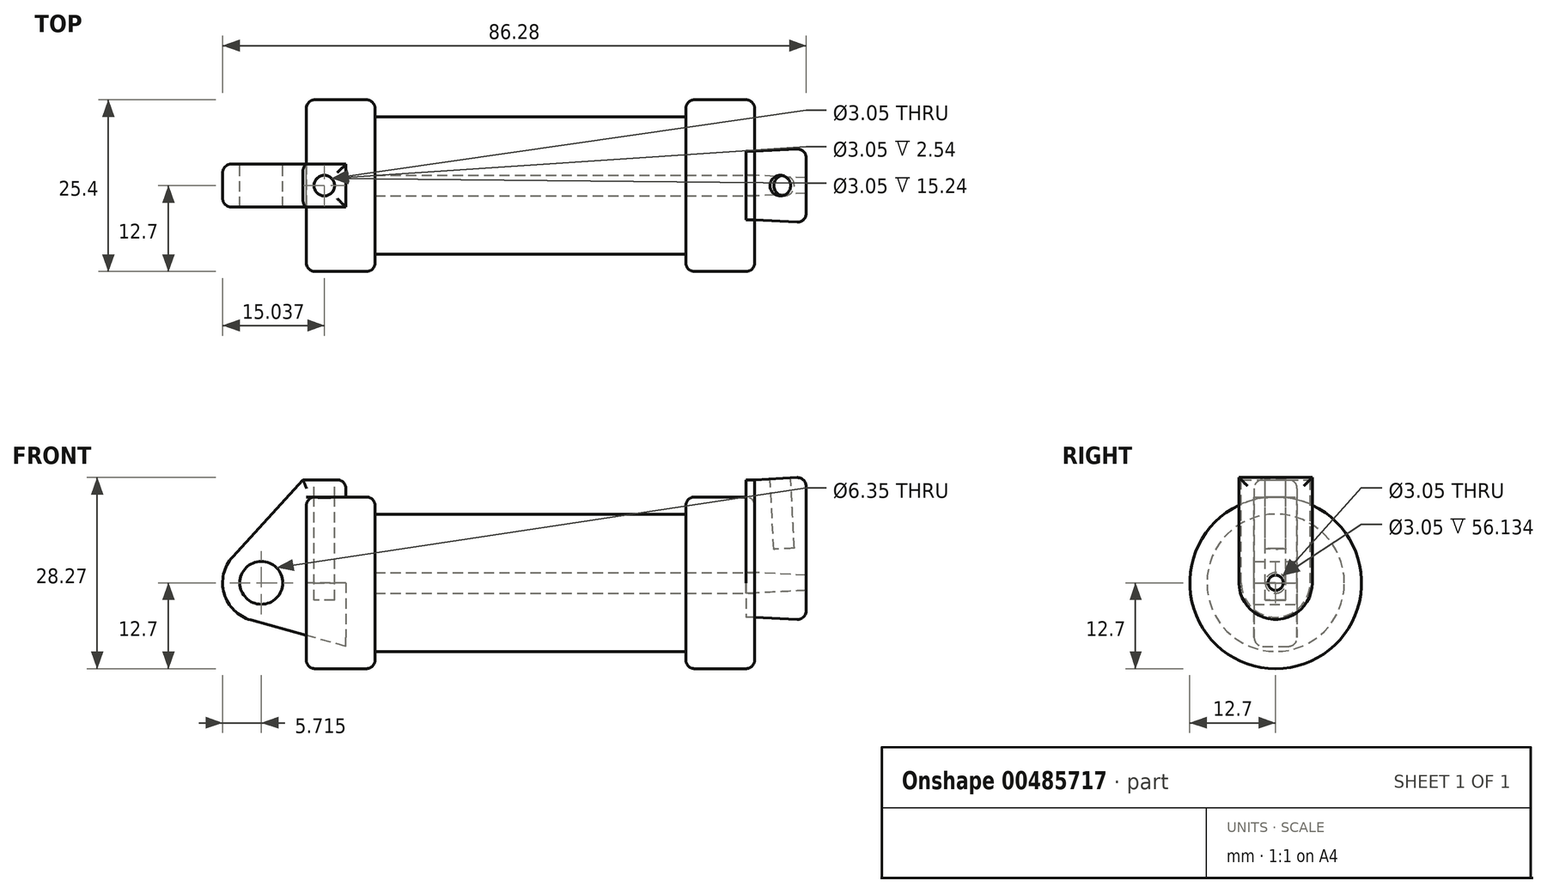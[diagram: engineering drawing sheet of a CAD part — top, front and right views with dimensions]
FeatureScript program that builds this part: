
annotation { "Feature Type Name" : "Feature", "Feature Type Description" : "" }
export const myFeature = defineFeature(function(context is Context, id is Id, definition is map)
    precondition{}
    {
        {
            var Q0;
            Q0=qCreatedBy(makeId("Front.planeOp"),FACE);
            var sketch = newSketch(context, id + "F0", { "sketchPlane" : qUnion([Q0])});
            skLineSegment(sketch, "E0", {"start": v(0, 0) * mm, "end": v(0, 12.7) * mm});
            skLineSegment(sketch, "E1", {"start": v(0, 12.7) * mm, "end": v(10.16, 12.7) * mm});
            skLineSegment(sketch, "E2", {"start": v(10.16, 12.7) * mm, "end": v(10.16, 10.16) * mm});
            skLineSegment(sketch, "E3", {"start": v(10.16, 10.16) * mm, "end": v(56.13, 10.16) * mm});
            skLineSegment(sketch, "E4", {"start": v(56.13, 10.16) * mm, "end": v(56.13, 12.7) * mm});
            skLineSegment(sketch, "E5", {"start": v(56.13, 12.7) * mm, "end": v(66.3, 12.7) * mm});
            skLineSegment(sketch, "E6", {"start": v(66.3, 12.7) * mm, "end": v(66.3, 0) * mm});
            skLineSegment(sketch, "E7", {"start": v(66.3, 0) * mm, "end": v(0, 0) * mm});
            skLineSegment(sketch, "E8", {"start": v(5.84, 15.24) * mm, "end": v(-0.5, 15.24) * mm});
            skLineSegment(sketch, "E9", {"start": v(-0.5, 15.24) * mm, "end": v(-10.88, 3.85) * mm});
            skLineSegment(sketch, "E10", {"start": v(0, 0) * mm, "end": v(-6.65, 0) * mm});
            skCircle(sketch, "E11", {"center": v(-6.65, 0) * mm, "radius": 5.72 * mm});
            skCircle(sketch, "E12", {"center": v(-6.65, 0) * mm, "radius": 3.18 * mm});
            skLineSegment(sketch, "E13", {"start": v(5.84, 15.24) * mm, "end": v(5.84, -9.4) * mm});
            skLineSegment(sketch, "E14", {"start": v(5.84, -9.4) * mm, "end": v(-8.18, -5.5) * mm});
            skSolve(sketch);
        }
        {
            var Q0;
            {var subQ0=sQuery(id+"F0.wireOp",EDGE,"E2");Q0=makeQuery(id+"F0.imprint","IMPRINT",FACE,{"disambiguationData":[TD([[makeQuery(id+"F0.imprint","IMPRINT",EDGE,{"derivedFrom":subQ0}),-1.0]])]});}
            var Q1;
            {var subQ0=sQuery(id+"F0.wireOp",EDGE,"E0");Q1=makeQuery(id+"F0.imprint","IMPRINT",FACE,{"disambiguationData":[TD([[makeQuery(id+"F0.imprint","IMPRINT",EDGE,{"derivedFrom":subQ0}),-1.0]])]});}
            var Q2;
            Q2=sQuery(id+"F0.wireOp",EDGE,"E7");
            revolve(context, id + "F1", {"entities" : qUnion([Q0, Q1]), "axis" : qUnion([Q2]), "revolveType" : RevolveType.FULL});
        }
        {
            var Q0;
            {var subQ5=sQuery(id+"F0.wireOp",EDGE,"E12");Q0=makeQuery(id+"F0.imprint","IMPRINT",FACE,{"disambiguationData":[TD([[makeQuery(id+"F0.imprint","IMPRINT",EDGE,{"derivedFrom":subQ5}),-1.0]])]});}
            var Q1;
            {var subQ1=sQuery(id+"F0.wireOp",EDGE,"E0");Q1=makeQuery(id+"F0.imprint","IMPRINT",FACE,{"disambiguationData":[TD([[makeQuery(id+"F0.imprint","IMPRINT",EDGE,{"derivedFrom":subQ1}),1.0]])]});}
            var Q2;
            {var subQ0=sQuery(id+"F0.wireOp",EDGE,"E14");Q2=makeQuery(id+"F0.imprint","IMPRINT",FACE,{"disambiguationData":[TD([[makeQuery(id+"F0.imprint","IMPRINT",EDGE,{"derivedFrom":subQ0}),-1.0]])]});}
            extrude(context, id + "F2", {"entities" : qUnion([Q0, Q1, Q2]), "endBound" : BoundingType.SYMMETRIC, "depth" : 6.35 * mm});
        }
        {
            var Q0;
            Q0=makeQuery(id+"F1.opRevolve","SWEPT_FACE",FACE,{"disambiguationData":[OSD([sQuery(id+"F0.wireOp",EDGE,"E6")])]});
            var sketch = newSketch(context, id + "F3", { "sketchPlane" : qUnion([Q0])});
            skCircle(sketch, "E15", {"center": v(0, 0) * mm, "radius": 1.52 * mm});
            skCircle(sketch, "E16", {"center": v(0, 0) * mm, "radius": 5.08 * mm});
            skLineSegment(sketch, "E17", {"start": v(-5.08, 0) * mm, "end": v(-5.08, 15.24) * mm});
            skLineSegment(sketch, "E18", {"start": v(-5.08, 15.24) * mm, "end": v(5.08, 15.24) * mm});
            skLineSegment(sketch, "E19", {"start": v(5.08, 15.24) * mm, "end": v(5.08, 0) * mm});
            skSolve(sketch);
        }
        {
            var Q0;
            Q0=makeQuery(id+"F3.imprint","IMPRINT",FACE,{"disambiguationData":[TD([[makeQuery(id+"F3.imprint","IMPRINT",EDGE,{"derivedFrom":sQuery(id+"F3.wireOp",EDGE,"E15")}),-1.0]])]});
            var Q1;
            {var subQ0=sQuery(id+"F3.wireOp",EDGE,"E17");var subQ1=sQuery(id+"F3.wireOp",EDGE,"E16");var subQ2=makeQuery(id+"F3.imprint","INTERSECT",VERTEX,{"derivedFrom":[subQ1,subQ0]});Q1=makeQuery(id+"F3.imprint","IMPRINT",FACE,{"disambiguationData":[TD([[makeQuery(id+"F3.imprint","IMPRINT",EDGE,{"disambiguationData":[TD([[subQ2,1.0]])],"derivedFrom":subQ1}),-1.0]])]});}
            var Q2;
            {var subQ0=sQuery(id+"F3.wireOp",EDGE,"E18");Q2=makeQuery(id+"F3.imprint","IMPRINT",FACE,{"disambiguationData":[TD([[makeQuery(id+"F3.imprint","IMPRINT",EDGE,{"derivedFrom":subQ0}),-1.0]])]});}
            extrude(context, id + "F4", {"entities" : qUnion([Q0, Q1, Q2]), "depth" : 7.62 * mm, "hasDraft" : true, "draftAngle" : 3 * degree, "hasSecondDirection" : true, "secondDirectionOppositeDirection" : true, "secondDirectionDepth" : 1.27 * mm});
        }
        {
            var Q0;
            Q0=makeQuery(id+"F3.imprint","IMPRINT",FACE,{"disambiguationData":[TD([[makeQuery(id+"F3.imprint","IMPRINT",EDGE,{"derivedFrom":sQuery(id+"F3.wireOp",EDGE,"E15")}),1.0]])]});
            var Q1;
            Q1=makeQuery(id+"F1.opRevolve","SWEPT_FACE",FACE,{"disambiguationData":[OSD([sQuery(id+"F0.wireOp",EDGE,"E2")])]});
            extrude(context, id + "F5", {"entities" : qUnion([Q0]), "operationType" : NewBodyOperationType.REMOVE, "endBound" : BoundingType.UP_TO_SURFACE, "oppositeDirection" : true, "endBoundEntityFace" : qUnion([Q1]), "depth" : 25.4 * mm});
        }
        {
            var Q0;
            Q0=makeQuery(id+"F4.*.split.splitOp","SPLIT",FACE,{"derivedFrom":makeQuery(id+"F4.opExtrude","SWEPT_FACE",FACE,{"disambiguationData":[OSD([sQuery(id+"F3.wireOp",EDGE,"E18")])]})});
            var sketch = newSketch(context, id + "F6", { "sketchPlane" : qUnion([Q0])});
            skCircle(sketch, "E20", {"center": v(70.82, 0) * mm, "radius": 1.52 * mm});
            skPoint(sketch, "E20.centerSnap0", {"position": v(70.82, 5.28) * mm});
            skPoint(sketch, "E20.centerSnap1", {"position": v(74.63, 0) * mm});
            skSolve(sketch);
        }
        {
            var Q0;
            Q0=makeQuery(id+"F6.imprint","IMPRINT",FACE,{"disambiguationData":[TD([[makeQuery(id+"F6.imprint","IMPRINT",EDGE,{"derivedFrom":sQuery(id+"F6.wireOp",EDGE,"E20")}),1.0]])]});
            extrude(context, id + "F7", {"entities" : qUnion([Q0]), "operationType" : NewBodyOperationType.REMOVE, "oppositeDirection" : true, "depth" : 10.4 * mm});
        }
        {
            var Q0;
            Q0=makeQuery(id+"F2.opExtrude","SWEPT_FACE",FACE,{"disambiguationData":[OSD([sQuery(id+"F0.wireOp",EDGE,"E8")])]});
            var sketch = newSketch(context, id + "F8", { "sketchPlane" : qUnion([Q0])});
            skCircle(sketch, "E21", {"center": v(2.67, 0) * mm, "radius": 1.52 * mm});
            skPoint(sketch, "E21.centerSnap0", {"position": v(2.67, 3.18) * mm});
            skPoint(sketch, "E21.centerSnap1", {"position": v(5.84, 0) * mm});
            skSolve(sketch);
        }
        {
            var Q0;
            Q0=makeQuery(id+"F8.imprint","IMPRINT",FACE,{"disambiguationData":[TD([[makeQuery(id+"F8.imprint","IMPRINT",EDGE,{"derivedFrom":sQuery(id+"F8.wireOp",EDGE,"E21")}),1.0]])]});
            extrude(context, id + "F9", {"entities" : qUnion([Q0]), "operationType" : NewBodyOperationType.REMOVE, "oppositeDirection" : true, "depth" : 17.78 * mm});
        }
        {
            var Q0;
            Q0=makeQuery(id+"F1.opRevolve","SWEPT_EDGE",EDGE,{"disambiguationData":[OSD([sQuery(id+"F0.wireOp",EDGE,"E1"),sQuery(id+"F0.wireOp",EDGE,"E2")])]});
            var Q1;
            Q1=makeQuery(id+"F1.opRevolve","SWEPT_EDGE",EDGE,{"disambiguationData":[OSD([sQuery(id+"F0.wireOp",EDGE,"E0"),sQuery(id+"F0.wireOp",EDGE,"E1")])]});
            var Q2;
            Q2=makeQuery(id+"F2.opExtrude","CAP_EDGE",EDGE,{"disambiguationData":[OSD([sQuery(id+"F0.wireOp",EDGE,"E8")])],"isStart":false});
            var Q3;
            Q3=makeQuery(id+"F2.opExtrude","SWEPT_EDGE",EDGE,{"disambiguationData":[OSD([sQuery(id+"F0.wireOp",EDGE,"E8"),sQuery(id+"F0.wireOp",EDGE,"E13")])]});
            var Q4;
            Q4=makeQuery(id+"F2.opExtrude","CAP_EDGE",EDGE,{"disambiguationData":[OSD([sQuery(id+"F0.wireOp",EDGE,"E8")])],"isStart":true});
            var Q5;
            Q5=makeQuery(id+"F2.opExtrude","CAP_EDGE",EDGE,{"disambiguationData":[OSD([sQuery(id+"F0.wireOp",EDGE,"E9")])],"isStart":false});
            var Q6;
            Q6=makeQuery(id+"F2.opExtrude","CAP_EDGE",EDGE,{"disambiguationData":[OSD([sQuery(id+"F0.wireOp",EDGE,"E9")])],"isStart":true});
            var Q7;
            Q7=makeQuery(id+"F1.opRevolve","SWEPT_EDGE",EDGE,{"disambiguationData":[OSD([sQuery(id+"F0.wireOp",EDGE,"E4"),sQuery(id+"F0.wireOp",EDGE,"E5")])]});
            var Q8;
            Q8=makeQuery(id+"F1.opRevolve","SWEPT_EDGE",EDGE,{"disambiguationData":[OSD([sQuery(id+"F0.wireOp",EDGE,"E5"),sQuery(id+"F0.wireOp",EDGE,"E6")])]});
            var Q9;
            Q9=makeQuery(id+"F4.opExtrude","CAP_EDGE",EDGE,{"disambiguationData":[OSD([sQuery(id+"F3.wireOp",EDGE,"E19")])],"isStart":false});
            var Q10;
            Q10=makeQuery(id+"F4.opExtrude","CAP_EDGE",EDGE,{"disambiguationData":[OSD([sQuery(id+"F3.wireOp",EDGE,"E18")])],"isStart":false});
            fillet(context, id + "F10", {"entities" : qUnion([Q0, Q1, Q2, Q3, Q4, Q5, Q6, Q7, Q8, Q9, Q10]), "radius" : 1.27 * mm, "tangentPropagation" : true, "allowEdgeOverflow" : false});
        }
    });
